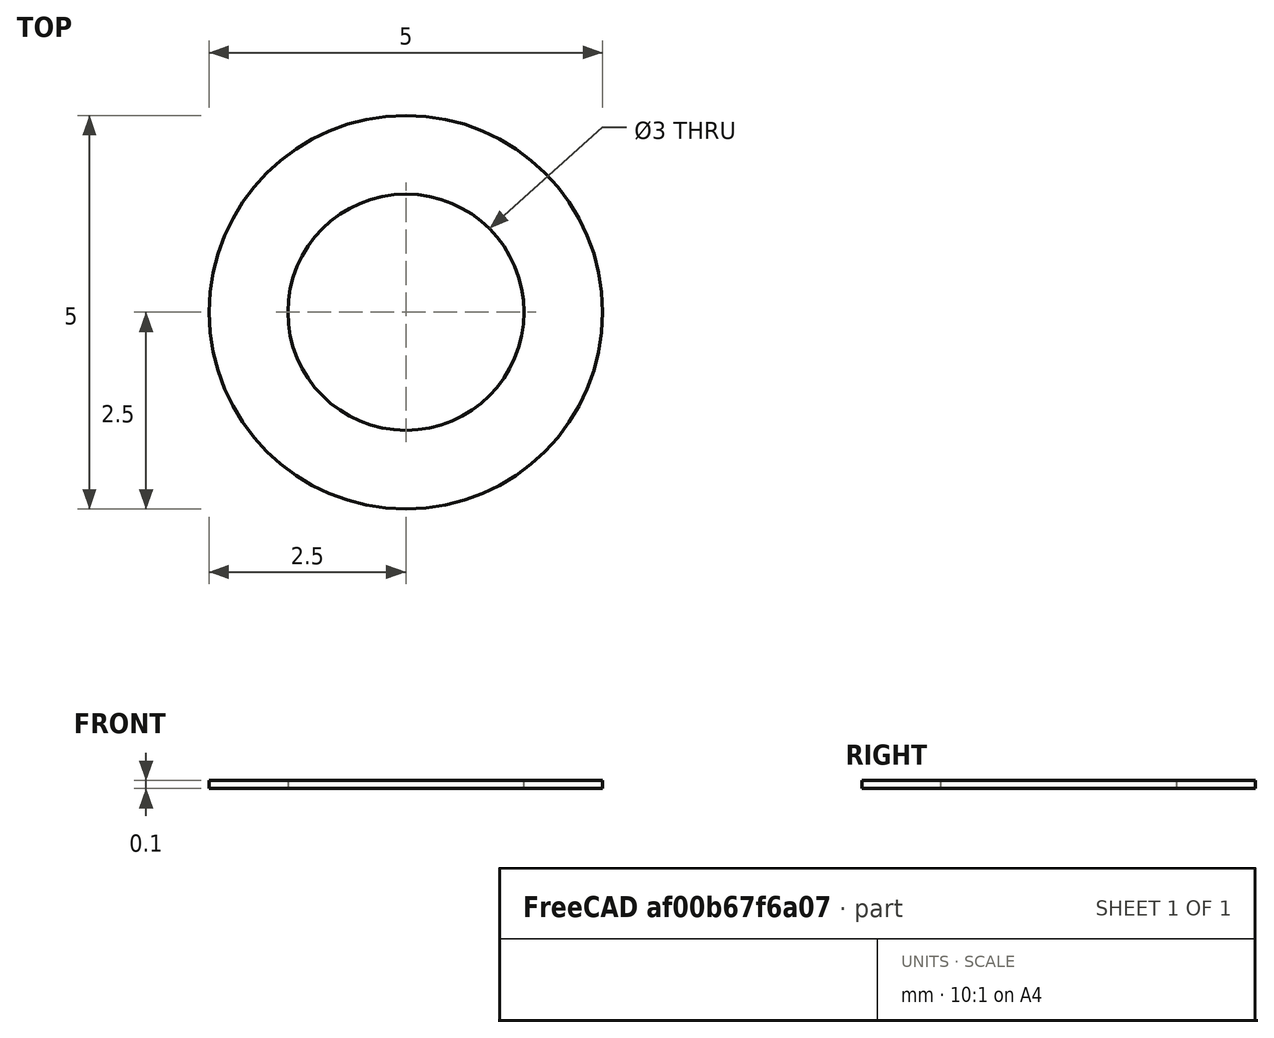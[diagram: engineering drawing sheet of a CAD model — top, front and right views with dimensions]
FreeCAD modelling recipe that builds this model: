
FCSTD DOCUMENT  (FreeCAD 0.21R33668 +26 (Git))
Label: shimring_d3D5h01
License: All rights reserved
LicenseURL: http://en.wikipedia.org/wiki/All_rights_reserved
objects: Sketcher::SketchObject×1, PartDesign::Pad×1, PartDesign::Body×1
note: 4 computed .brp shape members not serialized (recipe doc carries the construction recipe); baked Part::Feature solids carry a one-line shape summary decoded from their .brp

FEATURE [Sketcher::SketchObject] Sketch
  FullyConstrained = true
  MapMode = 5
  Support = -> [XY_Plane]
  sketch-geometry (2):
    g0: Circle CenterX=0 CenterY=0 CenterZ=0 NormalX=0 NormalY=0 NormalZ=1 AngleXU=0 Radius=1.5
    g1: Circle CenterX=0 CenterY=0 CenterZ=0 NormalX=0 NormalY=0 NormalZ=1 AngleXU=0 Radius=2.5
  constraints (4):
    c: Coincident(g0,g-1)
    c: Coincident(g1,g0)
    c: Diameter(g0) = 3
    c: Diameter(g1) = 5
FEATURE [PartDesign::Pad] Pad
  Direction = (0,0,1)
  Length = 0.1
  Length2 = 10
  Profile = -> Sketch
  ReferenceAxis = -> Sketch [N_Axis]
  Type = 0
FEATURE [PartDesign::Body] Body
  Group = -> [Sketch,Pad]
  Origin = -> Origin
  Tip = -> Pad
